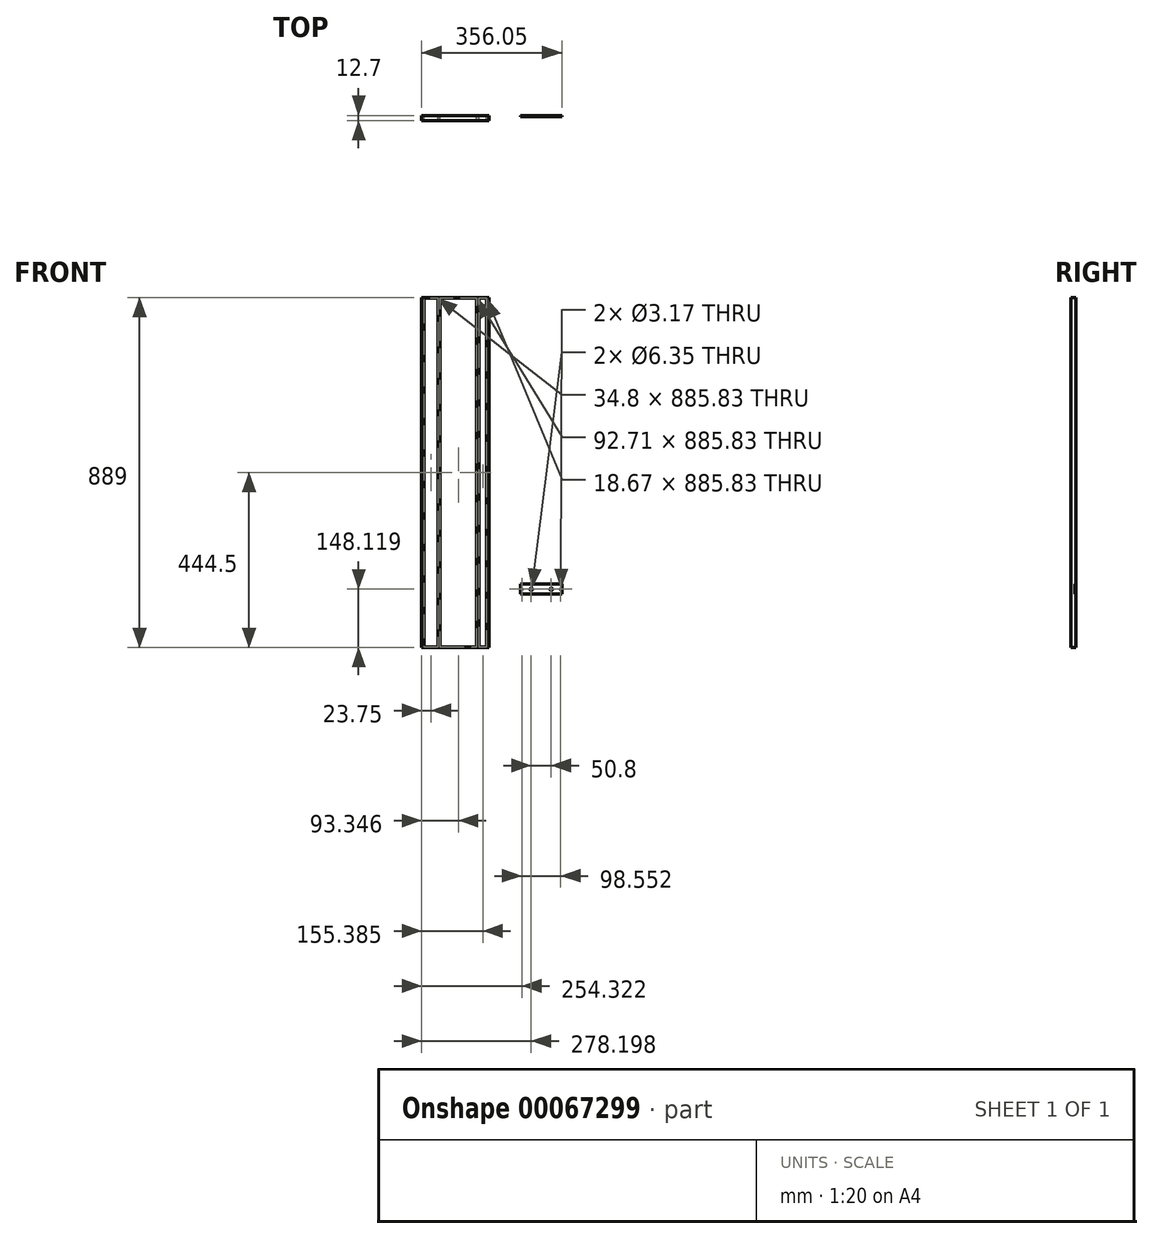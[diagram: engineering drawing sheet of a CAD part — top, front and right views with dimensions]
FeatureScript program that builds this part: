
annotation { "Feature Type Name" : "Feature", "Feature Type Description" : "" }
export const myFeature = defineFeature(function(context is Context, id is Id, definition is map)
    precondition{}
    {
        {
            var Q0;
            Q0=qCreatedBy(makeId("Front.planeOp"),FACE);
            var sketch = newSketch(context, id + "F0", { "sketchPlane" : qUnion([Q0])});
            skLineSegment(sketch, "E0.bottom", {"start": v(0, 0) * mm, "end": v(-171.07, 0) * mm});
            skLineSegment(sketch, "E0.top", {"start": v(0, 889) * mm, "end": v(-171.07, 889) * mm});
            skLineSegment(sketch, "E0.left", {"start": v(0, 0) * mm, "end": v(0, 889) * mm});
            skLineSegment(sketch, "E0.right", {"start": v(-171.07, 0) * mm, "end": v(-171.07, 889) * mm});
            skLineSegment(sketch, "E1", {"start": v(-164.72, 889) * mm, "end": v(-164.72, 0) * mm});
            skLineSegment(sketch, "E2", {"start": v(-129.92, 889) * mm, "end": v(-129.92, 0) * mm});
            skLineSegment(sketch, "E3", {"start": v(-124.08, 0) * mm, "end": v(-124.08, 889) * mm});
            skLineSegment(sketch, "E4", {"start": v(-31.37, 889) * mm, "end": v(-31.37, 0) * mm});
            skLineSegment(sketch, "E5", {"start": v(-25.02, 889) * mm, "end": v(-25.02, 0) * mm});
            skLineSegment(sketch, "E6", {"start": v(-6.35, 889) * mm, "end": v(-6.35, 0) * mm});
            skLineSegment(sketch, "E7", {"start": v(-171.07, 887.41) * mm, "end": v(0, 887.41) * mm});
            skLineSegment(sketch, "E8", {"start": v(-171.07, 1.59) * mm, "end": v(0, 1.59) * mm});
            skSolve(sketch);
        }
        {
            var Q0;
            {var subQ0=sQuery(id+"F0.wireOp",EDGE,"E7");var subQ1=sQuery(id+"F0.wireOp",EDGE,"E0.right");var subQ2=makeQuery(id+"F0.imprint","INTERSECT",VERTEX,{"derivedFrom":[subQ1,subQ0]});Q0=makeQuery(id+"F0.imprint","IMPRINT",FACE,{"disambiguationData":[TD([[makeQuery(id+"F0.imprint","IMPRINT",EDGE,{"disambiguationData":[TD([[subQ2,1.0]])],"derivedFrom":subQ1}),-1.0]])]});}
            var Q1;
            {var subQ0=sQuery(id+"F0.wireOp",EDGE,"E7");var subQ1=sQuery(id+"F0.wireOp",EDGE,"E2");var subQ2=makeQuery(id+"F0.imprint","INTERSECT",VERTEX,{"derivedFrom":[subQ1,subQ0]});Q1=makeQuery(id+"F0.imprint","IMPRINT",FACE,{"disambiguationData":[TD([[makeQuery(id+"F0.imprint","IMPRINT",EDGE,{"disambiguationData":[TD([[subQ2,-1.0]])],"derivedFrom":subQ1}),1.0]])]});}
            var Q2;
            {var subQ0=sQuery(id+"F0.wireOp",EDGE,"E7");var subQ1=sQuery(id+"F0.wireOp",EDGE,"E4");var subQ2=makeQuery(id+"F0.imprint","INTERSECT",VERTEX,{"derivedFrom":[subQ1,subQ0]});Q2=makeQuery(id+"F0.imprint","IMPRINT",FACE,{"disambiguationData":[TD([[makeQuery(id+"F0.imprint","IMPRINT",EDGE,{"disambiguationData":[TD([[subQ2,-1.0]])],"derivedFrom":subQ1}),1.0]])]});}
            var Q3;
            {var subQ0=sQuery(id+"F0.wireOp",EDGE,"E7");var subQ1=sQuery(id+"F0.wireOp",EDGE,"E0.left");var subQ2=makeQuery(id+"F0.imprint","INTERSECT",VERTEX,{"derivedFrom":[subQ1,subQ0]});Q3=makeQuery(id+"F0.imprint","IMPRINT",FACE,{"disambiguationData":[TD([[makeQuery(id+"F0.imprint","IMPRINT",EDGE,{"disambiguationData":[TD([[subQ2,1.0]])],"derivedFrom":subQ1}),1.0]])]});}
            var Q4;
            {var subQ0=sQuery(id+"F0.wireOp",EDGE,"E0.left");var subQ1=sQuery(id+"F0.wireOp",EDGE,"E0.top");var subQ2=makeQuery(id+"F0.imprint","INTERSECT",VERTEX,{"derivedFrom":[subQ1,subQ0]});Q4=makeQuery(id+"F0.imprint","IMPRINT",FACE,{"disambiguationData":[TD([[makeQuery(id+"F0.imprint","IMPRINT",EDGE,{"disambiguationData":[TD([[subQ2,-1.0]])],"derivedFrom":subQ1}),1.0]])]});}
            var Q5;
            {var subQ0=sQuery(id+"F0.wireOp",EDGE,"E5");var subQ1=sQuery(id+"F0.wireOp",EDGE,"E0.top");var subQ2=makeQuery(id+"F0.imprint","INTERSECT",VERTEX,{"derivedFrom":[subQ1,subQ0]});Q5=makeQuery(id+"F0.imprint","IMPRINT",FACE,{"disambiguationData":[TD([[makeQuery(id+"F0.imprint","IMPRINT",EDGE,{"disambiguationData":[TD([[subQ2,1.0]])],"derivedFrom":subQ1}),1.0]])]});}
            var Q6;
            {var subQ0=sQuery(id+"F0.wireOp",EDGE,"E3");var subQ1=sQuery(id+"F0.wireOp",EDGE,"E0.top");var subQ2=makeQuery(id+"F0.imprint","INTERSECT",VERTEX,{"derivedFrom":[subQ1,subQ0]});Q6=makeQuery(id+"F0.imprint","IMPRINT",FACE,{"disambiguationData":[TD([[makeQuery(id+"F0.imprint","IMPRINT",EDGE,{"disambiguationData":[TD([[subQ2,1.0]])],"derivedFrom":subQ1}),1.0]])]});}
            var Q7;
            {var subQ0=sQuery(id+"F0.wireOp",EDGE,"E2");var subQ1=sQuery(id+"F0.wireOp",EDGE,"E0.top");var subQ2=makeQuery(id+"F0.imprint","INTERSECT",VERTEX,{"derivedFrom":[subQ1,subQ0]});Q7=makeQuery(id+"F0.imprint","IMPRINT",FACE,{"disambiguationData":[TD([[makeQuery(id+"F0.imprint","IMPRINT",EDGE,{"disambiguationData":[TD([[subQ2,1.0]])],"derivedFrom":subQ1}),1.0]])]});}
            var Q8;
            {var subQ0=sQuery(id+"F0.wireOp",EDGE,"E1");var subQ1=sQuery(id+"F0.wireOp",EDGE,"E0.top");var subQ2=makeQuery(id+"F0.imprint","INTERSECT",VERTEX,{"derivedFrom":[subQ1,subQ0]});Q8=makeQuery(id+"F0.imprint","IMPRINT",FACE,{"disambiguationData":[TD([[makeQuery(id+"F0.imprint","IMPRINT",EDGE,{"disambiguationData":[TD([[subQ2,1.0]])],"derivedFrom":subQ1}),1.0]])]});}
            var Q9;
            {var subQ0=sQuery(id+"F0.wireOp",EDGE,"E0.right");var subQ1=sQuery(id+"F0.wireOp",EDGE,"E0.top");var subQ2=makeQuery(id+"F0.imprint","INTERSECT",VERTEX,{"derivedFrom":[subQ1,subQ0]});Q9=makeQuery(id+"F0.imprint","IMPRINT",FACE,{"disambiguationData":[TD([[makeQuery(id+"F0.imprint","IMPRINT",EDGE,{"disambiguationData":[TD([[subQ2,1.0]])],"derivedFrom":subQ1}),1.0]])]});}
            var Q10;
            {var subQ0=sQuery(id+"F0.wireOp",EDGE,"E4");var subQ1=sQuery(id+"F0.wireOp",EDGE,"E0.top");var subQ2=makeQuery(id+"F0.imprint","INTERSECT",VERTEX,{"derivedFrom":[subQ1,subQ0]});Q10=makeQuery(id+"F0.imprint","IMPRINT",FACE,{"disambiguationData":[TD([[makeQuery(id+"F0.imprint","IMPRINT",EDGE,{"disambiguationData":[TD([[subQ2,1.0]])],"derivedFrom":subQ1}),1.0]])]});}
            var Q11;
            {var subQ0=sQuery(id+"F0.wireOp",EDGE,"E0.right");var subQ1=sQuery(id+"F0.wireOp",EDGE,"E0.bottom");var subQ2=makeQuery(id+"F0.imprint","INTERSECT",VERTEX,{"derivedFrom":[subQ1,subQ0]});Q11=makeQuery(id+"F0.imprint","IMPRINT",FACE,{"disambiguationData":[TD([[makeQuery(id+"F0.imprint","IMPRINT",EDGE,{"disambiguationData":[TD([[subQ2,1.0]])],"derivedFrom":subQ1}),-1.0]])]});}
            var Q12;
            {var subQ0=sQuery(id+"F0.wireOp",EDGE,"E1");var subQ1=sQuery(id+"F0.wireOp",EDGE,"E0.bottom");var subQ2=makeQuery(id+"F0.imprint","INTERSECT",VERTEX,{"derivedFrom":[subQ1,subQ0]});Q12=makeQuery(id+"F0.imprint","IMPRINT",FACE,{"disambiguationData":[TD([[makeQuery(id+"F0.imprint","IMPRINT",EDGE,{"disambiguationData":[TD([[subQ2,1.0]])],"derivedFrom":subQ1}),-1.0]])]});}
            var Q13;
            {var subQ0=sQuery(id+"F0.wireOp",EDGE,"E2");var subQ1=sQuery(id+"F0.wireOp",EDGE,"E0.bottom");var subQ2=makeQuery(id+"F0.imprint","INTERSECT",VERTEX,{"derivedFrom":[subQ1,subQ0]});Q13=makeQuery(id+"F0.imprint","IMPRINT",FACE,{"disambiguationData":[TD([[makeQuery(id+"F0.imprint","IMPRINT",EDGE,{"disambiguationData":[TD([[subQ2,1.0]])],"derivedFrom":subQ1}),-1.0]])]});}
            var Q14;
            {var subQ0=sQuery(id+"F0.wireOp",EDGE,"E3");var subQ1=sQuery(id+"F0.wireOp",EDGE,"E0.bottom");var subQ2=makeQuery(id+"F0.imprint","INTERSECT",VERTEX,{"derivedFrom":[subQ1,subQ0]});Q14=makeQuery(id+"F0.imprint","IMPRINT",FACE,{"disambiguationData":[TD([[makeQuery(id+"F0.imprint","IMPRINT",EDGE,{"disambiguationData":[TD([[subQ2,1.0]])],"derivedFrom":subQ1}),-1.0]])]});}
            var Q15;
            {var subQ0=sQuery(id+"F0.wireOp",EDGE,"E5");var subQ1=sQuery(id+"F0.wireOp",EDGE,"E0.bottom");var subQ2=makeQuery(id+"F0.imprint","INTERSECT",VERTEX,{"derivedFrom":[subQ1,subQ0]});Q15=makeQuery(id+"F0.imprint","IMPRINT",FACE,{"disambiguationData":[TD([[makeQuery(id+"F0.imprint","IMPRINT",EDGE,{"disambiguationData":[TD([[subQ2,1.0]])],"derivedFrom":subQ1}),-1.0]])]});}
            var Q16;
            {var subQ0=sQuery(id+"F0.wireOp",EDGE,"E4");var subQ1=sQuery(id+"F0.wireOp",EDGE,"E0.bottom");var subQ2=makeQuery(id+"F0.imprint","INTERSECT",VERTEX,{"derivedFrom":[subQ1,subQ0]});Q16=makeQuery(id+"F0.imprint","IMPRINT",FACE,{"disambiguationData":[TD([[makeQuery(id+"F0.imprint","IMPRINT",EDGE,{"disambiguationData":[TD([[subQ2,1.0]])],"derivedFrom":subQ1}),-1.0]])]});}
            var Q17;
            {var subQ0=sQuery(id+"F0.wireOp",EDGE,"E0.left");var subQ1=sQuery(id+"F0.wireOp",EDGE,"E0.bottom");var subQ2=makeQuery(id+"F0.imprint","INTERSECT",VERTEX,{"derivedFrom":[subQ1,subQ0]});Q17=makeQuery(id+"F0.imprint","IMPRINT",FACE,{"disambiguationData":[TD([[makeQuery(id+"F0.imprint","IMPRINT",EDGE,{"disambiguationData":[TD([[subQ2,-1.0]])],"derivedFrom":subQ1}),-1.0]])]});}
            extrude(context, id + "F1", {"entities" : qUnion([Q0, Q1, Q2, Q3, Q4, Q5, Q6, Q7, Q8, Q9, Q10, Q11, Q12, Q13, Q14, Q15, Q16, Q17]), "depth" : 12.7 * mm});
        }
        {
            var Q0;
            Q0=qCreatedBy(makeId("Front.planeOp"),FACE);
            var sketch = newSketch(context, id + "F2", { "sketchPlane" : qUnion([Q0])});
            skLineSegment(sketch, "E9.bottom", {"start": v(80.08, 160.82) * mm, "end": v(184.98, 160.82) * mm});
            skLineSegment(sketch, "E9.top", {"start": v(80.08, 135.42) * mm, "end": v(184.98, 135.42) * mm});
            skLineSegment(sketch, "E9.left", {"start": v(80.08, 160.82) * mm, "end": v(80.08, 135.42) * mm});
            skLineSegment(sketch, "E9.right", {"start": v(184.98, 160.82) * mm, "end": v(184.98, 135.42) * mm});
            skLineSegment(sketch, "E10", {"start": v(132.53, 160.82) * mm, "end": v(132.53, 135.42) * mm, "construction": true});
            skCircle(sketch, "E11", {"center": v(83.25, 148.12) * mm, "radius": 1.59 * mm});
            skLineSegment(sketch, "E12", {"start": v(80.08, 148.12) * mm, "end": v(184.98, 148.12) * mm, "construction": true});
            skCircle(sketch, "E13.MirrorC", {"center": v(181.8, 148.12) * mm, "radius": 1.59 * mm});
            skCircle(sketch, "E14", {"center": v(107.13, 148.12) * mm, "radius": 3.18 * mm});
            skCircle(sketch, "E15.MirrorC", {"center": v(157.93, 148.12) * mm, "radius": 3.18 * mm});
            skSolve(sketch);
        }
        {
            var Q0;
            Q0=makeQuery(id+"F2.imprint","IMPRINT",FACE,{"disambiguationData":[TD([[makeQuery(id+"F2.imprint","IMPRINT",EDGE,{"derivedFrom":sQuery(id+"F2.wireOp",EDGE,"E9.bottom")}),-1.0]])]});
            extrude(context, id + "F3", {"entities" : qUnion([Q0]), "depth" : 3.17 * mm});
        }
    });
